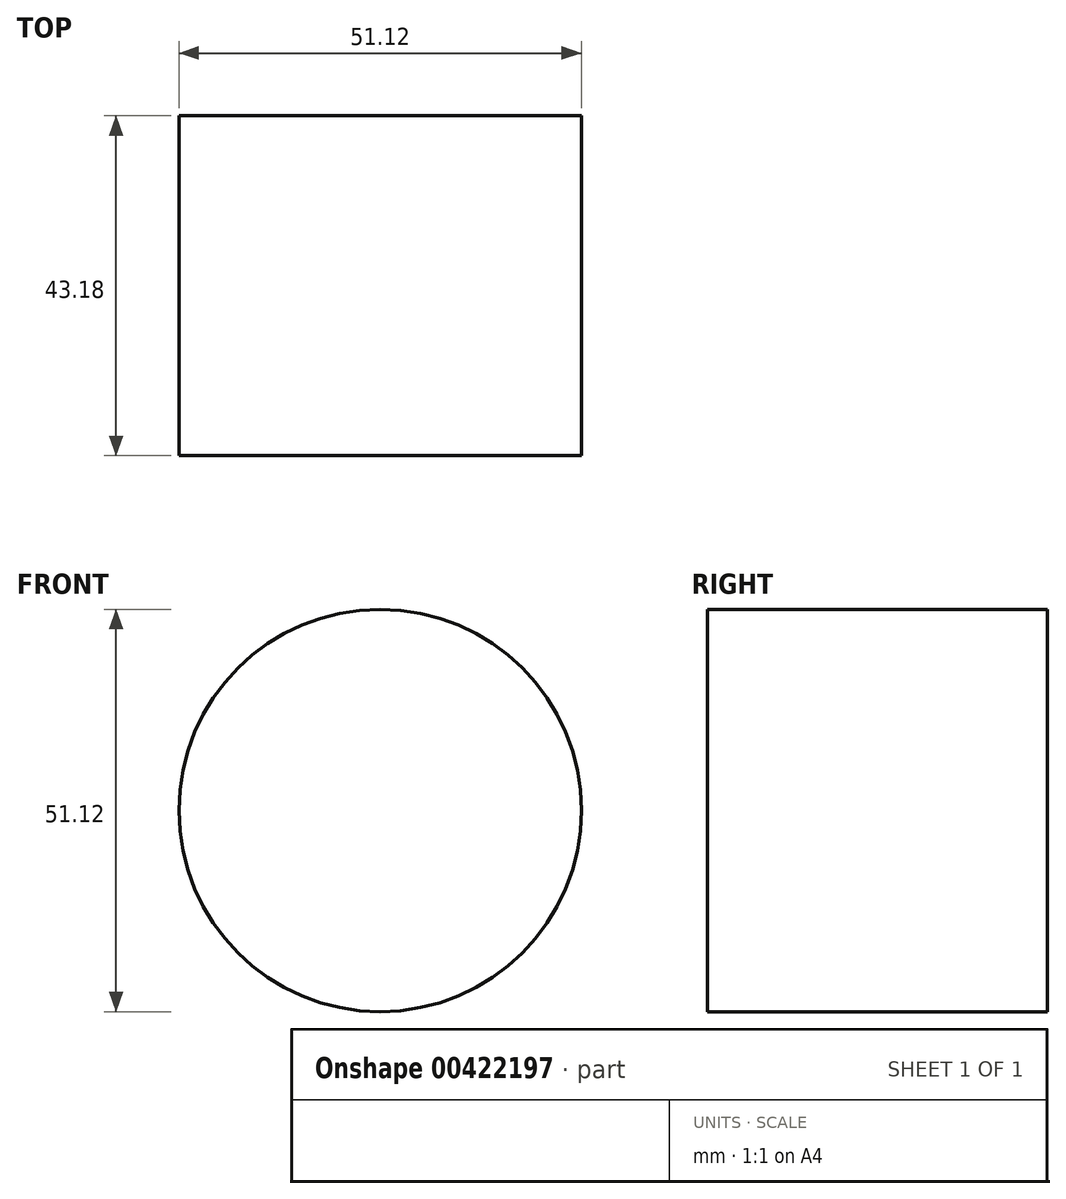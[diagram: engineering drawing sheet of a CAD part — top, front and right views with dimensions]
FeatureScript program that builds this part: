
annotation { "Feature Type Name" : "Feature", "Feature Type Description" : "" }
export const myFeature = defineFeature(function(context is Context, id is Id, definition is map)
    precondition{}
    {
        {
            var Q0;
            Q0=qCreatedBy(makeId("Front.planeOp"),FACE);
            var sketch = newSketch(context, id + "F0", { "sketchPlane" : qUnion([Q0])});
            skCircle(sketch, "E0", {"center": v(0, 0) * mm, "radius": 25.56 * mm});
            skSolve(sketch);
        }
        {
            var Q0;
            Q0 = qSketchRegion(id + "F0", true);
            extrude(context, id + "F1", {"entities" : qUnion([Q0]), "depth" : 43.18 * mm});
        }
    });
